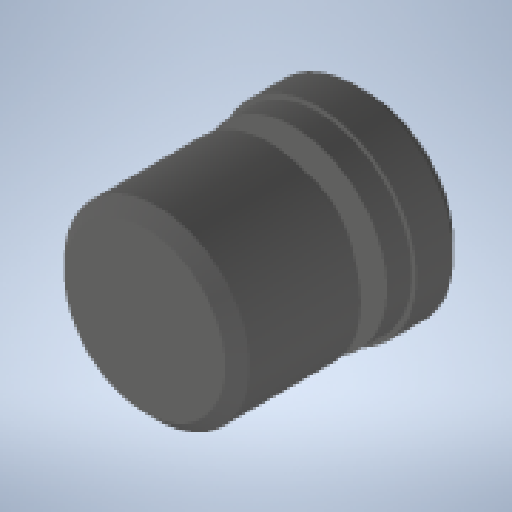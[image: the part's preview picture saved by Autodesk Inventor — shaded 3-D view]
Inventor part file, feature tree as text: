
AUTODESK INVENTOR PART (.ipt)
format: ipt  version: 2023.2 (Build 272271000, 271)  size: 172,544 bytes
history: native  units: mm
features: extrude x4, sketch x4, chamfer x2
ambient origin geometry x8: Origin, YZ Plane, XZ Plane, XY Plane, X Axis, Y Axis, Z Axis, Center Point
bodies: Solid1 (feature_tree)
feature tree (10):
  extrude  "Extrusion1"  Depth=5.0mm TaperAngle=0.0deg
  chamfer  "Chamfer1"  Distance=2.0mm Angle=45.0deg
  extrude  "Extrusion2"  Depth=1.0mm TaperAngle=0.0deg
  extrude  "Extrusion3"  Depth=1.0mm TaperAngle=0.0deg
  extrude  "Extrusion4"  Depth=2.0mm TaperAngle=45.0deg
  chamfer  "Chamfer2"  Distance=0.5mm
  sketch  "Sketch1"  dims[d0=7.5mm d1=5.0mm d2=0.0mm d3=0.5mm d4=2.0mm d5=45.0deg]
  sketch  "Sketch2"  dims[d6=5.0mm d7=1.0mm d8=0.0mm]
  sketch  "Sketch3"  dims[d9=7.6mm d10=1.0mm d11=0.0mm]
  sketch  "Sketch4"  dims[d12=2.0mm d13=0.0mm d14=0.5mm d15=2.0mm d16=45.0deg d17=0.5mm d18=0.872665mm d19=0.5mm d20=0.872665mm]
